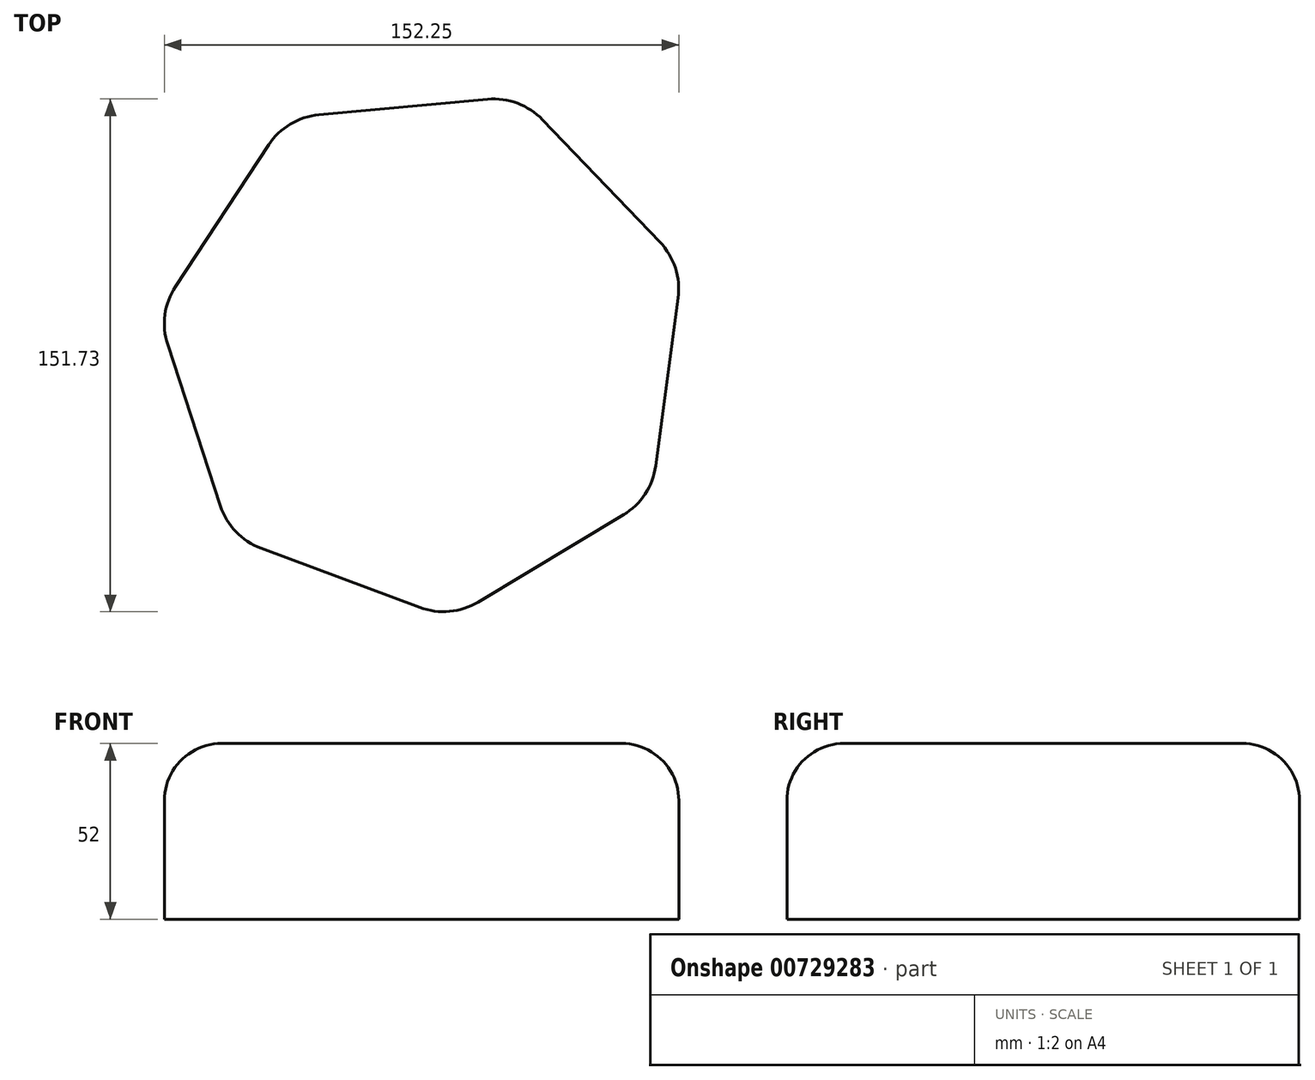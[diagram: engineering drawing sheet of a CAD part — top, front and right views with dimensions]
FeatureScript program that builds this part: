
annotation { "Feature Type Name" : "Feature", "Feature Type Description" : "" }
export const myFeature = defineFeature(function(context is Context, id is Id, definition is map)
    precondition{}
    {
        {
            var Q0;
            Q0=qCreatedBy(makeId("Top.planeOp"),FACE);
            var sketch = newSketch(context, id + "F0", { "sketchPlane" : qUnion([Q0])});
            skCircle(sketch, "E0.cCircle", {"center": v(0, 0) * mm, "radius": 72.08 * mm, "construction": true});
            skLineSegment(sketch, "E0.0", {"start": v(-57.73, -55.4) * mm, "end": v(-79.3, 10.6) * mm});
            skLineSegment(sketch, "E0.1", {"start": v(-79.3, 10.6) * mm, "end": v(-41.16, 68.61) * mm});
            skLineSegment(sketch, "E0.2", {"start": v(-41.16, 68.61) * mm, "end": v(27.98, 74.96) * mm});
            skLineSegment(sketch, "E0.3", {"start": v(27.98, 74.96) * mm, "end": v(76.05, 24.86) * mm});
            skLineSegment(sketch, "E0.4", {"start": v(76.05, 24.86) * mm, "end": v(66.85, -43.96) * mm});
            skLineSegment(sketch, "E0.5", {"start": v(66.85, -43.96) * mm, "end": v(7.31, -79.67) * mm});
            skLineSegment(sketch, "E0.6", {"start": v(7.31, -79.67) * mm, "end": v(-57.73, -55.4) * mm});
            skPoint(sketch, "E0.0.midPoint", {"position": v(-68.52, -22.4) * mm});
            skSolve(sketch);
        }
        {
            var Q0;
            Q0=makeQuery(id+"F0.imprint","IMPRINT",FACE,{"disambiguationData":[TD([[makeQuery(id+"F0.imprint","IMPRINT",EDGE,{"derivedFrom":sQuery(id+"F0.wireOp",EDGE,"E0.0")}),-1.0]])]});
            extrude(context, id + "F1", {"entities" : qUnion([Q0]), "depth" : 52 * mm, "offsetDistance" : 25 * mm});
        }
        {
            var Q0;
            Q0=makeQuery(id+"F1.opExtrude","CAP_FACE",FACE,{"disambiguationData":[OSD([sQuery(id+"F0.wireOp",EDGE,"E0.0"),sQuery(id+"F0.wireOp",EDGE,"E0.1"),sQuery(id+"F0.wireOp",EDGE,"E0.2"),sQuery(id+"F0.wireOp",EDGE,"E0.3"),sQuery(id+"F0.wireOp",EDGE,"E0.4"),sQuery(id+"F0.wireOp",EDGE,"E0.5"),sQuery(id+"F0.wireOp",EDGE,"E0.6")])],"isStart":false});
            fillet(context, id + "F2", {"entities" : qUnion([Q0]), "radius" : 16.9 * mm, "tangentPropagation" : true, "allowEdgeOverflow" : false});
        }
        {
            var Q0;
            Q0=makeQuery(id+"F1.opExtrude","SWEPT_EDGE",EDGE,{"disambiguationData":[OSD([sQuery(id+"F0.wireOp",EDGE,"E0.5"),sQuery(id+"F0.wireOp",EDGE,"E0.6")])]});
            var Q1;
            Q1=makeQuery(id+"F1.opExtrude","SWEPT_EDGE",EDGE,{"disambiguationData":[OSD([sQuery(id+"F0.wireOp",EDGE,"E0.4"),sQuery(id+"F0.wireOp",EDGE,"E0.5")])]});
            var Q2;
            Q2=makeQuery(id+"F1.opExtrude","SWEPT_EDGE",EDGE,{"disambiguationData":[OSD([sQuery(id+"F0.wireOp",EDGE,"E0.3"),sQuery(id+"F0.wireOp",EDGE,"E0.4")])]});
            var Q3;
            Q3=makeQuery(id+"F1.opExtrude","SWEPT_EDGE",EDGE,{"disambiguationData":[OSD([sQuery(id+"F0.wireOp",EDGE,"E0.2"),sQuery(id+"F0.wireOp",EDGE,"E0.3")])]});
            var Q4;
            Q4=makeQuery(id+"F1.opExtrude","SWEPT_EDGE",EDGE,{"disambiguationData":[OSD([sQuery(id+"F0.wireOp",EDGE,"E0.1"),sQuery(id+"F0.wireOp",EDGE,"E0.2")])]});
            var Q5;
            Q5=makeQuery(id+"F1.opExtrude","SWEPT_EDGE",EDGE,{"disambiguationData":[OSD([sQuery(id+"F0.wireOp",EDGE,"E0.0"),sQuery(id+"F0.wireOp",EDGE,"E0.1")])]});
            var Q6;
            Q6=makeQuery(id+"F1.opExtrude","SWEPT_EDGE",EDGE,{"disambiguationData":[OSD([sQuery(id+"F0.wireOp",EDGE,"E0.0"),sQuery(id+"F0.wireOp",EDGE,"E0.6")])]});
            fillet(context, id + "F3", {"entities" : qUnion([Q0, Q1, Q2, Q3, Q4, Q5, Q6]), "radius" : 20 * mm, "tangentPropagation" : true, "allowEdgeOverflow" : false});
        }
    });
